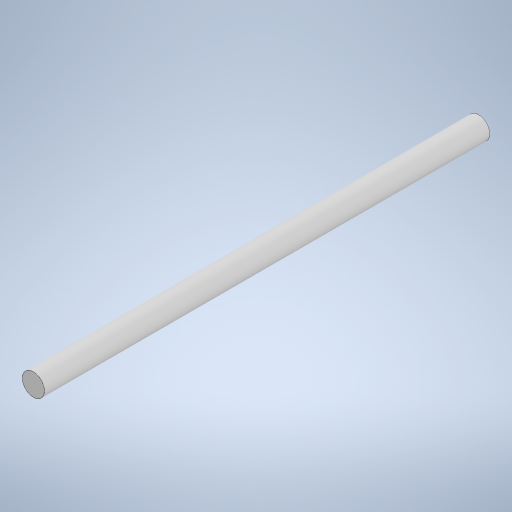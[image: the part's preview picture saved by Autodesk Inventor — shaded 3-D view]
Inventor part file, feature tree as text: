
AUTODESK INVENTOR PART (.ipt)
format: ipt  version: 2024 (Build 280153000, 153)  size: 230,400 bytes
history: native  units: mm
features: extrude x1, sketch x1
ambient origin geometry x8: Origin, YZ Plane, XZ Plane, XY Plane, X Axis, Y Axis, Z Axis, Center Point
bodies: Solid1 (feature_tree)
feature tree (2):
  extrude  "Extrusion1"  Depth=255.0mm TaperAngle=0.0deg
  sketch  "Sketch1"  dims[d0=12.7mm d1=255.0mm d2=0.0mm]
